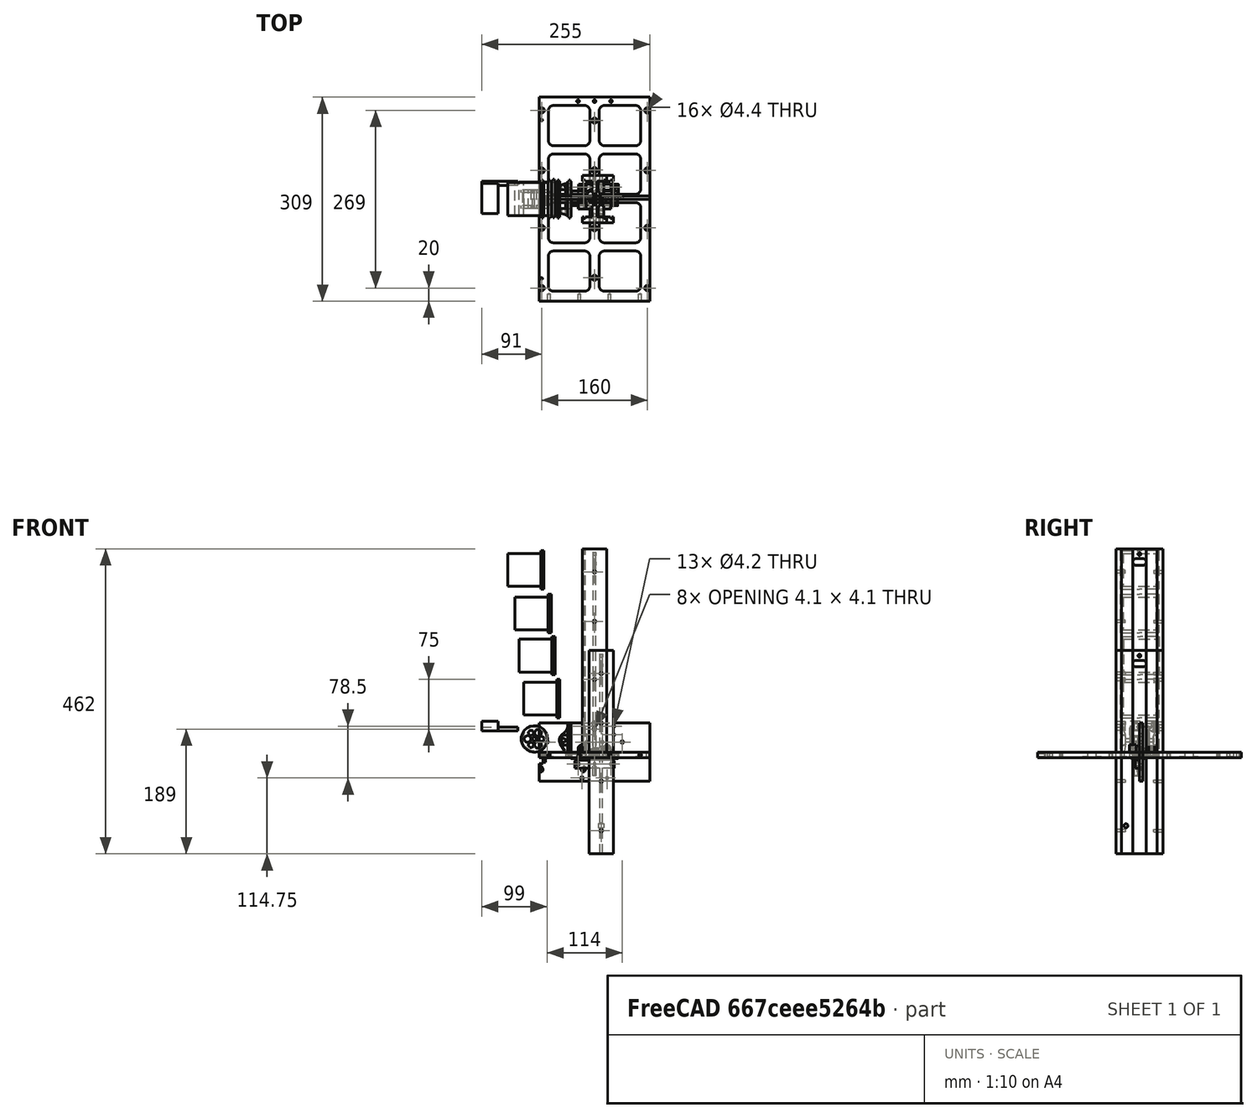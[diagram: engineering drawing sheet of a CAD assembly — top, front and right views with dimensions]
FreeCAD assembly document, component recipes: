
FREECAD ASSEMBLY — COMPONENT RECIPES ("simulation")

This assembly document has 7 components, labeled P0..P6 below (a component is one placed body or linked part). 3 of them carry a construction recipe — the FreeCAD feature program that regenerates the part from scratch, quoted from this document or its linked companion documents; the rest are supplied as boundary geometry only. No exploded tour is included for this assembly.
COMPONENT P0 — geometry summary ("door_001"; no construction recipe available for this part):
  bounding box: 168.0 x 88.5 x 8.0 mm
  tessellated surface: 8,896 triangles
  volume: 73640 mm^3 (62% of its bounding box)
COMPONENT P1 — geometry summary ("door_003"; no construction recipe available for this part):
  bounding box: 60.0 x 23.0 x 16.0 mm
  tessellated surface: 6,880 triangles
  volume: 10095 mm^3 (46% of its bounding box)
COMPONENT P2 — geometry summary ("door_004"; no construction recipe available for this part):
  bounding box: 80.0 x 5.0 x 5.0 mm
  tessellated surface: 500 triangles
  volume: 1571 mm^3 (79% of its bounding box)
  symmetry: 2-fold rotationally symmetric about the x axis; 2-fold rotationally symmetric about the y axis; 6-fold rotationally symmetric about the z axis; mirror-symmetric across its x mid-plane, y mid-plane
COMPONENT P3 — geometry summary ("door_005"; no construction recipe available for this part):
  bounding box: 16.0 x 12.0 x 8.0 mm
  tessellated surface: 15,084 triangles
  volume: 969 mm^3 (63% of its bounding box)
  symmetry: 2-fold rotationally symmetric about the z axis; mirror-symmetric across its y mid-plane
COMPONENT P4 — recipe-attached ("hinge_001", a linked part whose construction recipe lives in a companion FreeCAD document of the same project; that document's serialized recipe follows).
Construction recipe (the companion document, serialized — sketch geometry with constraints, then the solid features built on it; lengths are millimeters unless a unit is written):

FCSTD DOCUMENT  (FreeCAD 0.18R14555 (Git shallow))
Label: hinge
License: All rights reserved
LicenseURL: http://en.wikipedia.org/wiki/All_rights_reserved
objects: TechDraw::DrawViewDimension×17, Sketcher::SketchObject×11, PartDesign::Pocket×6, TechDraw::DrawProjGroupItem×6, PartDesign::Pad×3, TechDraw::DrawProjGroup×3, PartDesign::Body×3, PartDesign::Hole×2, TechDraw::DrawSVGTemplate×2, TechDraw::DrawViewAnnotation×2, TechDraw::DrawViewSymbol×2, TechDraw::DrawViewPart×2, TechDraw::DrawPage×2, PartDesign::Plane×1, PartDesign::Fillet×1, TechDraw::DrawViewSection×1
note: 38 computed .brp shape members not serialized (recipe doc carries the construction recipe); baked Part::Feature solids carry a one-line shape summary decoded from their .brp

FEATURE [Sketcher::SketchObject] Sketch001
  MapMode = 5
  Support = -> [XY_Plane001]
  sketch-geometry (8):
    g0: LineSegment StartX=-35 StartY=-10 StartZ=0 EndX=-35 EndY=12.5 EndZ=0
    g1: LineSegment StartX=-35 StartY=12.5 StartZ=0 EndX=35 EndY=12.5 EndZ=0
    g2: LineSegment StartX=35 StartY=12.5 StartZ=0 EndX=35 EndY=-10 EndZ=0
    g3: LineSegment StartX=35 StartY=-10 StartZ=0 EndX=25 EndY=-10 EndZ=0
    g4: LineSegment StartX=25 StartY=-10 StartZ=0 EndX=25 EndY=0 EndZ=0
    g5: LineSegment StartX=-35 StartY=-10 StartZ=0 EndX=-25 EndY=-10 EndZ=0
    g6: LineSegment StartX=-25 StartY=-10 StartZ=0 EndX=-25 EndY=0 EndZ=0
    g7: LineSegment StartX=-25 StartY=0 StartZ=0 EndX=25 EndY=0 EndZ=0
  constraints (22):
    c: Vertical(g0)
    c: Coincident(g0,g1)
    c: Coincident(g1,g2)
    c: Vertical(g2)
    c: Coincident(g2,g3)
    c: Horizontal(g3)
    c: Coincident(g3,g4)
    c: PointOnObject(g4,g-1)
    c: Coincident(g0,g5)
    c: Horizontal(g5)
    c: Coincident(g5,g6)
    c: PointOnObject(g6,g-1)
    c: Vertical(g6)
    c: Vertical(g4)
    c: Symmetric(g1,g0,g-2)
    c: Symmetric(g3,g5,g-2)
    c: Coincident(g7,g4)
    c: DistanceX(g5,g5) = 10
    c: DistanceY(g6,g6) = 10
    c: Coincident(g7,g6)
    c: DistanceX(g5,g3) = 50
    c: DistanceY(g-1,g1) = 12.5
FEATURE [PartDesign::Pad] Pad001
  Length = 10
  Length2 = 100
  Profile = -> Sketch001
  Reversed = true
  Type = 0
FEATURE [Sketcher::SketchObject] Sketch002
  MapMode = 5
  Placement = pos=(0,0,0) rot=(0.57735,0.57735,0.57735;2.0944rad)
  Support = -> [YZ_Plane001]
  sketch-geometry (10):
    g0: Circle CenterX=-5 CenterY=-5 CenterZ=0 NormalX=0 NormalY=0 NormalZ=1 AngleXU=0 Radius=2.5
    g1: ArcOfCircle CenterX=-5 CenterY=-5 CenterZ=0 NormalX=0 NormalY=0 NormalZ=1 AngleXU=0 Radius=5 StartAngle=1.5708 EndAngle=3.14159
    g2: LineSegment [constr] StartX=-10 StartY=-5 StartZ=0 EndX=-10 EndY=0 EndZ=0
    g3: LineSegment StartX=-10 StartY=0 StartZ=0 EndX=-5 EndY=0 EndZ=0
    g4: LineSegment StartX=-10 StartY=-10 StartZ=0 EndX=-5 EndY=-10 EndZ=0
    g5: ArcOfCircle CenterX=-5 CenterY=-5 CenterZ=0 NormalX=0 NormalY=0 NormalZ=1 AngleXU=0 Radius=5 StartAngle=3.14159 EndAngle=4.71239
    g6: LineSegment [constr] StartX=-10 StartY=-5 StartZ=0 EndX=-10 EndY=-10 EndZ=0
    g7: LineSegment StartX=-10 StartY=0 StartZ=0 EndX=-13 EndY=0 EndZ=0
    g8: LineSegment StartX=-13 StartY=0 StartZ=0 EndX=-13 EndY=-10 EndZ=0
    g9: LineSegment StartX=-13 StartY=-10 StartZ=0 EndX=-10 EndY=-10 EndZ=0
  constraints (27):
    c: Diameter(g0) = 5
    c: Coincident(g1,g0)
    c: Vertical(g2)
    c: Coincident(g3,g2)
    c: Tangent(g3,g1) = 1.5708
    c: Coincident(g1,g3)
    c: Horizontal(g3)
    c: DistanceX(g0,g-1) = 5
    c: PointOnObject(g2,g-1)
    c: DistanceY(g0,g-1) = 5
    c: Horizontal(g4)
    c: Tangent(g1,g5) = -1.5708
    c: Tangent(g1,g2) = 1.5708
    c: Coincident(g6,g1)
    c: Vertical(g6)
    c: Coincident(g4,g6)
    c: Equal(g6,g2)
    c: Coincident(g3,g7)
    c: Coincident(g7,g8)
    c: Vertical(g8)
    c: Coincident(g8,g9)
    c: Coincident(g9,g4)
    c: Horizontal(g9)
    c: Horizontal(g7)
    c: DistanceX(g1,g0) = 5
    c: DistanceX(g9,g9) = 3
    c: Tangent(g5,g4) = -1.5708
FEATURE [PartDesign::Pocket] Pocket
  BaseFeature = -> Pad001
  Length = 5
  Length2 = 100
  Midplane = true
  Profile = -> Sketch002
  Type = 1
FEATURE [Sketcher::SketchObject] Sketch007
  MapMode = 5
  Support = -> [XY_Plane001]
  sketch-geometry (5):
    g0: Circle [constr] CenterX=0 CenterY=6 CenterZ=0 NormalX=0 NormalY=0 NormalZ=1 AngleXU=0 Radius=2.1
    g1: Circle CenterX=25 CenterY=6 CenterZ=0 NormalX=0 NormalY=0 NormalZ=1 AngleXU=0 Radius=2.1
    g2: Circle CenterX=-25 CenterY=6 CenterZ=0 NormalX=0 NormalY=0 NormalZ=1 AngleXU=0 Radius=2.1
    g3: LineSegment [constr] StartX=0 StartY=6 StartZ=0 EndX=25 EndY=6 EndZ=0
    g4: LineSegment [constr] StartX=0 StartY=6 StartZ=0 EndX=-25 EndY=6 EndZ=0
  constraints (13):
    c: PointOnObject(g0,g-2)
    c: Coincident(g3,g0)
    c: Coincident(g3,g1)
    c: Coincident(g4,g0)
    c: Coincident(g4,g2)
    c: Horizontal(g3)
    c: Horizontal(g4)
    c: Equal(g4,g3)
    c: DistanceX(g2,g1) = 50
    c: Diameter(g0) = 4.2
    c: Equal(g0,g1)
    c: Equal(g0,g2)
    c: DistanceY(g-1,g0) = 6
FEATURE [PartDesign::Hole] Hole
  BaseFeature = -> Pocket
  Depth = 25
  DepthType = 1
  Diameter = 4.2
  DrillPoint = 1
  DrillPointAngle = 118
  HoleCutCountersinkAngle = 90
  HoleCutDepth = 0
  HoleCutDiameter = 0
  HoleCutType = 0
  ModelActualThread = false
  Profile = -> Sketch007
  Tapered = false
  TaperedAngle = 90
  ThreadAngle = 0
  ThreadClass = 0
  ThreadCutOffInner = 0
  ThreadCutOffOuter = 0
  ThreadDirection = 0
  ThreadFit = 0
  ThreadPitch = 0
  ThreadSize = 0
  ThreadType = 0
  Threaded = false
FEATURE [Sketcher::SketchObject] Sketch
  MapMode = 5
  Placement = pos=(0,0,0) rot=(0.57735,0.57735,0.57735;2.0944rad)
  Support = -> [YZ_Plane]
  sketch-geometry (7):
    g0: Circle CenterX=-5 CenterY=-5 CenterZ=0 NormalX=0 NormalY=0 NormalZ=1 AngleXU=0 Radius=2.5
    g1: ArcOfCircle CenterX=-5 CenterY=-5 CenterZ=0 NormalX=0 NormalY=0 NormalZ=1 AngleXU=0 Radius=5 StartAngle=4.71239 EndAngle=7.85398
    g2: LineSegment StartX=-4.99997 StartY=12 StartZ=0 EndX=-15 EndY=12 EndZ=0
    g3: LineSegment StartX=-15 StartY=12 StartZ=0 EndX=-15 EndY=-5 EndZ=0
    g4: LineSegment StartX=-9.99997 StartY=-10 StartZ=0 EndX=-5 EndY=-10 EndZ=0
    g5: LineSegment StartX=-4.99997 StartY=-8.94778e-11 StartZ=0 EndX=-4.99997 EndY=12 EndZ=0
    g6: ArcOfCircle CenterX=-9.99997 CenterY=-5 CenterZ=0 NormalX=0 NormalY=0 NormalZ=1 AngleXU=0 Radius=5 StartAngle=3.14159 EndAngle=4.71239
  constraints (20):
    c: DistanceX(g0,g-1) = 5
    c: DistanceY(g0,g-1) = 5
    c: Diameter(g0) = 5
    c: Coincident(g1,g0)
    c: PointOnObject(g1,g-1)
    c: Radius(g1) = 5
    c: Horizontal(g2)
    c: Coincident(g2,g3)
    c: Vertical(g3)
    c: Coincident(g4,g1)
    c: Horizontal(g4)
    c: DistanceY(g1,g2) = 12
    c: DistanceY(g1,g0) = 5
    c: DistanceX(g2,g2) = 10
    c: Coincident(g5,g2)
    c: Vertical(g5)
    c: Tangent(g4,g6) = -1.5708
    c: Tangent(g3,g6) = -1.5708
    c: Radius(g6) = 5
    c: Coincident(g5,g1)
FEATURE [PartDesign::Pad] Pad
  Length = 50
  Length2 = 100
  Midplane = true
  Placement = pos=(0,0,0) rot=(0.57735,0.57735,0.57735;2.0944rad)
  Profile = -> Sketch
  Type = 0
FEATURE [Sketcher::SketchObject] Sketch010
  MapMode = 5
  Placement = pos=(0,0,0) rot=(1,0,0;1.5708rad)
  Support = -> [XZ_Plane]
  sketch-geometry (14):
    g0: LineSegment StartX=13 StartY=5 StartZ=0 EndX=13 EndY=4 EndZ=0
    g1: LineSegment StartX=-13 StartY=4 StartZ=0 EndX=-13 EndY=5 EndZ=0
    g2: ArcOfCircle CenterX=-19 CenterY=5 CenterZ=0 NormalX=0 NormalY=0 NormalZ=1 AngleXU=0 Radius=6 StartAngle=1e-16 EndAngle=3.14159
    g3: ArcOfCircle CenterX=19 CenterY=5 CenterZ=0 NormalX=0 NormalY=0 NormalZ=1 AngleXU=0 Radius=6 StartAngle=0 EndAngle=3.14159
    g4: LineSegment [constr] StartX=25 StartY=5 StartZ=0 EndX=-25 EndY=5 EndZ=0
    g5: LineSegment StartX=25 StartY=5 StartZ=0 EndX=25 EndY=11 EndZ=0
    g6: LineSegment [constr] StartX=25 StartY=11 StartZ=0 EndX=-25 EndY=11 EndZ=0
    g7: LineSegment StartX=-25 StartY=11 StartZ=0 EndX=-25 EndY=5 EndZ=0
    g8: LineSegment StartX=-25 StartY=11 StartZ=0 EndX=-25 EndY=12 EndZ=0
    g9: LineSegment StartX=-25 StartY=12 StartZ=0 EndX=25 EndY=12 EndZ=0
    g10: LineSegment StartX=25 StartY=12 StartZ=0 EndX=25 EndY=11 EndZ=0
    g11: LineSegment StartX=-11 StartY=2 StartZ=0 EndX=11 EndY=2 EndZ=0
    g12: ArcOfCircle CenterX=-11 CenterY=4 CenterZ=0 NormalX=0 NormalY=0 NormalZ=1 AngleXU=0 Radius=2 StartAngle=3.14159 EndAngle=4.71239
    g13: ArcOfCircle CenterX=11 CenterY=4 CenterZ=0 NormalX=0 NormalY=0 NormalZ=1 AngleXU=0 Radius=2 StartAngle=4.71239 EndAngle=6.28319
  constraints (39):
    c: Vertical(g0)
    c: Vertical(g1)
    c: Symmetric(g0,g1,g-2)
    c: DistanceX(g1,g0) = 26
    c: Coincident(g2,g1)
    c: Coincident(g3,g0)
    c: Coincident(g4,g3)
    c: Coincident(g4,g2)
    c: Horizontal(g4)
    c: PointOnObject(g2,g4)
    c: PointOnObject(g1,g4)
    c: PointOnObject(g3,g4)
    c: Equal(g3,g2)
    c: DistanceX(g4,g4) = 50
    c: Coincident(g3,g5)
    c: Coincident(g5,g6)
    c: Horizontal(g6)
    c: Coincident(g6,g7)
    c: Coincident(g7,g2)
    c: Vertical(g7)
    c: DistanceY(g-1,g6) = 11
    c: Coincident(g7,g8)
    c: Vertical(g8)
    c: Coincident(g8,g9)
    c: Horizontal(g9)
    c: Coincident(g9,g10)
    c: Coincident(g10,g5)
    c: Vertical(g10)
    c: Vertical(g5)
    c: DistanceY(g8,g8) = 1
    c: Tangent(g2,g6)
    c: Horizontal(g11)
    c: Tangent(g1,g12) = 1.5708
    c: Tangent(g11,g12) = -1.5708
    c: Radius(g12) = 2
    c: DistanceY(g-1,g11) = 2
    c: Tangent(g0,g13) = 1.5708
    c: Tangent(g11,g13) = -1.5708
    c: Equal(g13,g12)
FEATURE [PartDesign::Plane] DatumPlane001
  AttachmentOffset = pos=(0,0,15) rot=(0,0,1;0rad)
  Length = 56.4768
  MapMode = 5
  Placement = pos=(0,-15,-3.3e-15) rot=(1,0,0;1.5708rad)
  ResizeMode = 0
  Support = -> [XZ_Plane]
  Width = 27.4512
FEATURE [Sketcher::SketchObject] Sketch011
  MapMode = 5
  Placement = pos=(0,-15,-3.3e-15) rot=(1,0,0;1.5708rad)
  Support = -> [DatumPlane001]
  sketch-geometry (2):
    g0: Circle CenterX=-19 CenterY=5 CenterZ=0 NormalX=0 NormalY=0 NormalZ=1 AngleXU=0 Radius=2
    g1: Circle CenterX=19 CenterY=5 CenterZ=0 NormalX=0 NormalY=0 NormalZ=1 AngleXU=0 Radius=2.31769
  constraints (4):
    c: Symmetric(g1,g0,g-2)
    c: DistanceX(g0,g1) = 38
    c: Diameter(g0) = 4
    c: DistanceY(g-1,g0) = 5
FEATURE [Sketcher::SketchObject] Sketch009
  MapMode = 5
  Placement = pos=(0,0,0) rot=(1,0,0;1.5708rad)
  Support = -> [XZ_Plane]
  sketch-geometry (6):
    g0: LineSegment StartX=-11.0007 StartY=0 StartZ=0 EndX=10.9993 EndY=0 EndZ=0
    g1: LineSegment StartX=12.9993 StartY=-2 StartZ=0 EndX=12.9993 EndY=-18.3189 EndZ=0
    g2: LineSegment StartX=12.9993 StartY=-18.3189 StartZ=0 EndX=-13.0007 EndY=-18.3189 EndZ=0
    g3: LineSegment StartX=-13.0007 StartY=-18.3189 StartZ=0 EndX=-13.0007 EndY=-2 EndZ=0
    g4: ArcOfCircle CenterX=10.9993 CenterY=-2 CenterZ=0 NormalX=0 NormalY=0 NormalZ=1 AngleXU=0 Radius=2 StartAngle=0 EndAngle=1.5708
    g5: ArcOfCircle CenterX=-11.0007 CenterY=-2 CenterZ=0 NormalX=0 NormalY=0 NormalZ=1 AngleXU=0 Radius=2 StartAngle=1.5708 EndAngle=3.14159
  constraints (14):
    c: Coincident(g1,g2)
    c: Coincident(g2,g3)
    c: Horizontal(g2)
    c: Vertical(g1)
    c: Vertical(g3)
    c: Tangent(g1,g4) = 1.5708
    c: Tangent(g0,g4) = 1.5708
    c: Tangent(g0,g5) = 1.5708
    c: Tangent(g3,g5) = 1.5708
    c: DistanceX(g3,g1) = 26
    c: Radius(g4) = 2
    c: Equal(g4,g5)
    c: Horizontal(g0)
    c: PointOnObject(g0,g-1)
FEATURE [PartDesign::Pocket] Pocket002
  BaseFeature = -> Pad
  Length = 10
  Length2 = 100
  Placement = pos=(0,0,0) rot=(0.57735,0.57735,0.57735;2.0944rad)
  Profile = -> Sketch009
  Reversed = true
  Type = 0
FEATURE [PartDesign::Pocket] Pocket003
  BaseFeature = -> Pocket002
  Length = 5
  Length2 = 100
  Placement = pos=(0,0,0) rot=(0.57735,0.57735,0.57735;2.0944rad)
  Profile = -> Sketch010
  Reversed = true
  Type = 1
FEATURE [TechDraw::DrawSVGTemplate] Template
  EditableTexts = Designed_by_Name=Papamatthaiou M.; FC-Date=17/01/2020; FC-SC=1:1; FC-SHEET=1/1; FC-Title=PocketQube Static Hinge; MATERIAL=NOTE-4; REV=B; ROUGHNESS=-; Subtitle=StatikHinge; TOLERANCES=DIN ISO 2768-mk; Weight=~26.56g
  Height = 210
  Orientation = 1
  Width = 297
FEATURE [TechDraw::DrawProjGroup] ProjGroup
  AutoDistribute = true
  LockPosition = false
  ProjectionType = 1
  Rotation = 0
  ScaleType = 2
  X = 168.228
  Y = 97.2357
  spacingX = 15
  spacingY = 15
FEATURE [TechDraw::DrawViewAnnotation] Annotation
  Font = DejaVu Sans
  LineSpace = 80
  LockPosition = false
  MaxWidth = -1
  Rotation = 0
  ScaleType = 0
  Text = Notes: | 1. Drill hole \u23004.2 THRU | 2. Mating hole (H7) for part P/N:  | MISUMI  SCLGN5-70 Shaft Dia. D: 5.00,  | Tolerance: g6 (sliding fit) | 3. This part is mating with parts DoorHinge | and with y-plate | 4. Material: Al 7075 | 5. Drill hole \u23001.5 THRU. Mating holes  | for torsional springs
  TextSize = 6
  TextStyle = 0
  X = 77.2478
  Y = 49.013
FEATURE [PartDesign::Hole] Hole001
  BaseFeature = -> Pocket003
  Depth = 25
  DepthType = 1
  Diameter = 4.5
  DrillPoint = 1
  DrillPointAngle = 118
  HoleCutCountersinkAngle = 90
  HoleCutDepth = 4.6
  HoleCutDiameter = 8
  HoleCutType = 1
  ModelActualThread = false
  Placement = pos=(0,0,0) rot=(0.57735,0.57735,0.57735;2.0944rad)
  Profile = -> Sketch011
  Tapered = false
  TaperedAngle = 90
  ThreadAngle = 0
  ThreadClass = 0
  ThreadCutOffInner = 0
  ThreadCutOffOuter = 0
  ThreadDirection = 0
  ThreadFit = 0
  ThreadPitch = 0
  ThreadSize = 0
  ThreadType = 0
  Threaded = false
FEATURE [TechDraw::DrawSVGTemplate] Template001
  EditableTexts = Designed_by_Name=Papamatthaiou M.; FC-Date=17/01/2020; FC-SC=1:1; FC-SHEET=1/1; FC-Title=PocketQube Door Hinge; MATERIAL=NOTE-5; REV=B; ROUGHNESS=-; Subtitle=DoorHinge; TOLERANCES=DIN ISO 2768-mk; Weight=~17.21g
  Height = 210
  Orientation = 1
  Width = 297
FEATURE [TechDraw::DrawViewSymbol] Symbol
  LockPosition = false
  Rotation = 0
  ScaleType = 2
  Symbol = <blob: 3150 chars omitted>
  X = 16.0884
  Y = 131.565
FEATURE [TechDraw::DrawViewSymbol] Symbol001
  LockPosition = false
  Rotation = 0
  ScaleType = 2
  Symbol = <blob: 3150 chars omitted>
  X = 22.4016
  Y = 147.366
FEATURE [TechDraw::DrawViewAnnotation] Annotation001
  Font = DejaVu Sans
  LineSpace = 80
  LockPosition = false
  MaxWidth = -1
  Rotation = 0
  ScaleType = 0
  Text = Notes: | 1. Drill hole \u23004.5 THRU | 2. Mating hole (H7) for part P/N:  | MISUMI  SCLGN5-70 Shaft Dia. D: 5.00,  | Tolerance: g6 (sliding fit) | 3. This part is mating with parts DoorHinge | and with door | 4. CBORE \u23008.00 DEEP 4.6 (M4 DIN912) | 5. Material: Al 7075 | 6. Drill Holes \u23001.5 THRU. Mating | holes for torsional springs
  TextSize = 6
  TextStyle = 0
  X = 77.0938
  Y = 51.4062
FEATURE [Sketcher::SketchObject] Sketch012
  MapMode = 5
  Placement = pos=(0,0,0) rot=(1,0,0;1.5708rad)
  Support = -> [XZ_Plane001]
  sketch-geometry (3):
    g0: Circle CenterX=-1.5 CenterY=-6.9 CenterZ=0 NormalX=0 NormalY=0 NormalZ=1 AngleXU=0 Radius=0.75
    g1: Circle CenterX=1.5 CenterY=-6.9 CenterZ=0 NormalX=0 NormalY=0 NormalZ=1 AngleXU=0 Radius=0.75
    g2: GeomPoint X=0 Y=-10 Z=0
  constraints (7):
    c: Diameter(g1) = 1.5
    c: Equal(g1,g0)
    c: Symmetric(g1,g0,g-2)
    c: DistanceX(g0,g1) = 3
    c: PointOnObject(g2,g-2)
    c: DistanceY(g2,g-1) = 10
    c: DistanceY(g2,g1) = 3.1
FEATURE [PartDesign::Pocket] Pocket004
  BaseFeature = -> Hole
  Length = 9
  Length2 = 100
  Profile = -> Sketch012
  Type = 0
FEATURE [PartDesign::Fillet] Fillet
  Base = -> Pocket004 [Edge19]
  BaseFeature = -> Pocket004
  Radius = 4
FEATURE [PartDesign::Body] Body001  label="StatikHinge"
  Group = -> [Sketch001,Pad001,Sketch002,Pocket,Sketch007,Hole,Sketch012,Pocket004,Fillet]
  Origin = -> Origin001
  Tip = -> Fillet
FEATURE [TechDraw::DrawViewPart] View
  CoarseView = false
  Direction = (0.831,-0.177,0.527)
  Focus = 100
  HardHidden = false
  IsoCount = 0
  IsoHidden = false
  IsoVisible = false
  LockPosition = false
  Perspective = false
  Rotation = 0
  ScaleType = 0
  SeamHidden = false
  SeamVisible = false
  SmoothHidden = false
  SmoothVisible = false
  Source = -> [Body001]
  X = 260.762
  Y = 173.153
FEATURE [Sketcher::SketchObject] Sketch013
  MapMode = 5
  Support = -> [XY_Plane]
  sketch-geometry (2):
    g0: Circle CenterX=-12.15 CenterY=-9.2 CenterZ=0 NormalX=0 NormalY=0 NormalZ=1 AngleXU=0 Radius=0.75
    g1: Circle CenterX=12.15 CenterY=-9.2 CenterZ=0 NormalX=0 NormalY=0 NormalZ=1 AngleXU=0 Radius=0.75
  constraints (5):
    c: Diameter(g1) = 1.5
    c: Equal(g1,g0)
    c: Symmetric(g0,g1,g-2)
    c: DistanceX(g0,g1) = 24.3
    c: DistanceY(g1,g-1) = 9.2
FEATURE [PartDesign::Pocket] Pocket005
  BaseFeature = -> Hole001
  Length = 5
  Length2 = 100
  Midplane = true
  Placement = pos=(0,0,0) rot=(0.57735,0.57735,0.57735;2.0944rad)
  Profile = -> Sketch013
  Type = 1
FEATURE [PartDesign::Body] Body  label="DoorHinge"
  Group = -> [Sketch,Pad,Sketch009,Pocket002,Sketch010,Pocket003,DatumPlane001,Sketch011,Hole001,Sketch013,Pocket005]
  Origin = -> Origin
  Tip = -> Pocket005
FEATURE [TechDraw::DrawProjGroupItem] ProjItem002  label="Front001"
  CoarseView = false
  Direction = (0,1,0)
  Focus = 100
  HardHidden = false
  IsoCount = 0
  IsoHidden = false
  IsoVisible = false
  LockPosition = true
  Perspective = false
  Rotation = 0
  RotationVector = (-1,0,0)
  ScaleType = 2
  SeamHidden = false
  SeamVisible = false
  SmoothHidden = false
  SmoothVisible = false
  Source = -> [Body]
  Type = 0
  X = 0
  Y = 0
FEATURE [TechDraw::DrawProjGroupItem] ProjItem003  label="Left001"
  CoarseView = false
  Direction = (1,1e-16,0)
  Focus = 100
  HardHidden = false
  IsoCount = 0
  IsoHidden = false
  IsoVisible = false
  LockPosition = false
  Perspective = false
  Rotation = 0
  RotationVector = (-1e-16,1,0)
  ScaleType = 2
  SeamHidden = false
  SeamVisible = false
  SmoothHidden = false
  SmoothVisible = false
  Source = -> [Body]
  Type = 1
  X = 65
  Y = 0
FEATURE [TechDraw::DrawViewDimension] Dimension007
  Arbitrary = false
  FormatSpec = (Note-1) ⌀%.2f
  LockPosition = false
  MeasureType = 1
  OverTolerance = 0
  References2D = -> [ProjItem002]
  Rotation = 0
  ScaleType = 0
  Type = 5
  UnderTolerance = 0
  X = 5.54075
  Y = 26.0395
FEATURE [TechDraw::DrawViewDimension] Dimension008
  Arbitrary = false
  FormatSpec = (Note-2) ⌀%.2fH7
  LockPosition = false
  MeasureType = 1
  OverTolerance = 0
  References2D = -> [ProjItem003]
  Rotation = 0
  ScaleType = 0
  Type = 5
  UnderTolerance = 0
  X = 38.605
  Y = 5.77784
FEATURE [TechDraw::DrawViewPart] View002
  CoarseView = false
  Direction = (-0.669,0.732,-0.128)
  Focus = 100
  HardHidden = false
  IsoCount = 0
  IsoHidden = false
  IsoVisible = false
  LockPosition = false
  Perspective = false
  Rotation = 0
  ScaleType = 0
  SeamHidden = false
  SeamVisible = false
  SmoothHidden = false
  SmoothVisible = false
  Source = -> [Body]
  X = 259.541
  Y = 183.599
FEATURE [TechDraw::DrawViewSection] DrawViewSection  label="Section B - B"
  BaseView = -> ProjItem002
  CoarseView = false
  Direction = (1,0,0)
  FileHatchPattern = <path>
  Focus = 100
  FuseBeforeCut = true
  HardHidden = false
  HatchScale = 1
  IsoCount = 0
  IsoHidden = false
  IsoVisible = false
  LockPosition = false
  NameGeomPattern = Diamond
  Perspective = false
  Rotation = 0
  ScaleType = 0
  SeamHidden = false
  SeamVisible = false
  SectionDirection = 0
  SectionNormal = (1,0,0)
  SectionOrigin = (-19,-7.5,0.5)
  SectionSymbol = B
  SmoothHidden = false
  SmoothVisible = false
  Source = -> [Body]
  X = 240.508
  Y = 105.408
FEATURE [TechDraw::DrawViewDimension] Dimension010
  Arbitrary = false
  FormatSpec = (Note-4) %.2f
  LockPosition = false
  MeasureType = 1
  OverTolerance = 0
  References2D = -> [DrawViewSection]
  Rotation = 0
  ScaleType = 0
  Type = 2
  UnderTolerance = 0
  X = -32.2034
  Y = -16.2929
FEATURE [TechDraw::DrawProjGroupItem] ProjItem004  label="Front002"
  CoarseView = false
  Direction = (0,0,1)
  Focus = 100
  HardHidden = false
  IsoCount = 0
  IsoHidden = false
  IsoVisible = false
  LockPosition = true
  Perspective = false
  Rotation = 0
  RotationVector = (1,0,0)
  ScaleType = 2
  SeamHidden = false
  SeamVisible = false
  SmoothHidden = false
  SmoothVisible = false
  Source = -> [Fillet]
  Type = 0
  X = 0
  Y = 0
FEATURE [TechDraw::DrawProjGroupItem] ProjItem005  label="Left002"
  CoarseView = false
  Direction = (-1,0,1e-16)
  Focus = 100
  HardHidden = false
  IsoCount = 0
  IsoHidden = false
  IsoVisible = false
  LockPosition = false
  Perspective = false
  Rotation = 0
  RotationVector = (1e-16,0,1)
  ScaleType = 2
  SeamHidden = false
  SeamVisible = false
  SmoothHidden = false
  SmoothVisible = false
  Source = -> [Fillet]
  Type = 1
  X = 85
  Y = 0
FEATURE [TechDraw::DrawViewDimension] Dimension012
  Arbitrary = false
  FormatSpec = (Note-3) %.2f
  LockPosition = false
  MeasureType = 1
  OverTolerance = 0.1
  References2D = -> [ProjItem004]
  Rotation = 0
  ScaleType = 0
  Type = 1
  UnderTolerance = 0
  X = -1.46419
  Y = -24.1349
FEATURE [TechDraw::DrawViewDimension] Dimension013
  Arbitrary = false
  FormatSpec = %.2f
  LockPosition = false
  MeasureType = 1
  OverTolerance = 0
  References2D = -> [ProjItem004]
  Rotation = 0
  ScaleType = 0
  Type = 1
  UnderTolerance = -0.2
  X = -2.04987
  Y = -35.5556
FEATURE [TechDraw::DrawProjGroupItem] ProjItem006  label="Bottom"
  CoarseView = false
  Direction = (0,-1,0)
  Focus = 100
  HardHidden = false
  IsoCount = 0
  IsoHidden = false
  IsoVisible = false
  LockPosition = false
  Perspective = false
  Rotation = 0
  RotationVector = (1,0,0)
  ScaleType = 2
  SeamHidden = false
  SeamVisible = false
  SmoothHidden = false
  SmoothVisible = false
  Source = -> [Fillet]
  Type = 5
  X = 0
  Y = 37.5
FEATURE [TechDraw::DrawProjGroup] ProjGroup002
  Anchor = -> ProjItem004
  AutoDistribute = true
  LockPosition = false
  ProjectionType = 1
  Rotation = 0
  ScaleType = 2
  Source = -> [Fillet]
  Views = -> [ProjItem004,ProjItem005,ProjItem006]
  X = 88.691
  Y = 138.45
  spacingX = 15
  spacingY = 15
FEATURE [TechDraw::DrawViewDimension] Dimension014
  Arbitrary = false
  FormatSpec = (Note-1) ⌀%.2f 
  LockPosition = false
  MeasureType = 1
  OverTolerance = 0
  References2D = -> [ProjItem004]
  Rotation = 0
  ScaleType = 0
  Type = 5
  UnderTolerance = 0
  X = 0.44554
  Y = 19.6037
FEATURE [TechDraw::DrawViewDimension] Dimension015
  Arbitrary = false
  FormatSpec = (Note-2) ⌀%.2fH7
  LockPosition = false
  MeasureType = 1
  OverTolerance = 0
  References2D = -> [ProjItem005]
  Rotation = 0
  ScaleType = 0
  Type = 5
  UnderTolerance = 0
  X = 32.9699
  Y = 6.01477
FEATURE [TechDraw::DrawViewDimension] Dimension016
  Arbitrary = false
  FormatSpec = %.2f
  LockPosition = false
  MeasureType = 1
  OverTolerance = 0.1
  References2D = -> [ProjItem005]
  Rotation = 0
  ScaleType = 0
  Type = 2
  UnderTolerance = -0.1
  X = -21.2176
  Y = 29.9006
FEATURE [TechDraw::DrawViewDimension] Dimension
  Arbitrary = false
  FormatSpec = %.2f
  LockPosition = false
  MeasureType = 1
  OverTolerance = 0.1
  References2D = -> [ProjItem006]
  Rotation = 0
  ScaleType = 0
  Type = 2
  UnderTolerance = 0
  X = -59.5871
  Y = 7.81223
FEATURE [TechDraw::DrawViewDimension] Dimension017
  Arbitrary = false
  FormatSpec = %.2f
  LockPosition = false
  MeasureType = 1
  OverTolerance = 0.1
  References2D = -> [ProjItem006]
  Rotation = 0
  ScaleType = 0
  Type = 1
  UnderTolerance = -0.1
  X = -20.6451
  Y = 17.6805
FEATURE [TechDraw::DrawViewDimension] Dimension018
  Arbitrary = false
  FormatSpec = (Note-5) ⌀%.2f
  LockPosition = false
  MeasureType = 1
  OverTolerance = 0
  References2D = -> [ProjItem006]
  Rotation = 0
  ScaleType = 0
  Type = 5
  UnderTolerance = 0
  X = 34.1246
  Y = 16.7219
FEATURE [TechDraw::DrawPage] Page
  KeepUpdated = true
  ProjectionType = 0
  Template = -> Template
  Views = -> [ProjGroup,View,Annotation,Symbol,ProjGroup002,Dimension012,Dimension013,Dimension014,Dimension015,Dimension016,Dimension,Dimension017,Dimension018]
FEATURE [TechDraw::DrawProjGroupItem] ProjItem007  label="Top"
  CoarseView = false
  Direction = (0,0,1)
  Focus = 100
  HardHidden = false
  IsoCount = 0
  IsoHidden = false
  IsoVisible = false
  LockPosition = true
  Perspective = false
  Rotation = 0
  RotationVector = (-1,0,0)
  ScaleType = 2
  SeamHidden = false
  SeamVisible = false
  SmoothHidden = false
  SmoothVisible = false
  Source = -> [Body]
  Type = 4
  X = 0
  Y = -42.1726
FEATURE [TechDraw::DrawProjGroup] ProjGroup001
  Anchor = -> ProjItem002
  AutoDistribute = true
  LockPosition = false
  ProjectionType = 1
  Rotation = 0
  ScaleType = 2
  Source = -> [Body]
  Views = -> [ProjItem002,ProjItem003,ProjItem007]
  X = 86.3263
  Y = 154.205
  spacingX = 15
  spacingY = 15
FEATURE [TechDraw::DrawViewDimension] Dimension019
  Arbitrary = false
  FormatSpec = (Note-3) %.2f
  LockPosition = false
  MeasureType = 1
  OverTolerance = 0
  References2D = -> [ProjItem002]
  Rotation = 0
  ScaleType = 0
  Type = 1
  UnderTolerance = -0.1
  X = -2.96872
  Y = -23.0803
FEATURE [TechDraw::DrawViewDimension] Dimension020
  Arbitrary = false
  FormatSpec = (Note-3) R%.2f
  LockPosition = false
  MeasureType = 1
  OverTolerance = 0
  References2D = -> [ProjItem003]
  Rotation = 0
  ScaleType = 0
  Type = 4
  UnderTolerance = -0.1
  X = 39.0019
  Y = -15.3008
FEATURE [TechDraw::DrawViewDimension] Dimension021
  Arbitrary = false
  FormatSpec = %.2f
  LockPosition = false
  MeasureType = 1
  OverTolerance = 0.1
  References2D = -> [ProjItem007]
  Rotation = 0
  ScaleType = 0
  Type = 1
  UnderTolerance = 0
  X = 3.06171
  Y = -19.944
FEATURE [TechDraw::DrawViewDimension] Dimension022
  Arbitrary = false
  FormatSpec = %.2f
  LockPosition = false
  MeasureType = 1
  OverTolerance = 0.1
  References2D = -> [ProjItem007]
  Rotation = 0
  ScaleType = 0
  Type = 2
  UnderTolerance = -0.1
  X = -52.0507
  Y = -9.25974
FEATURE [TechDraw::DrawViewDimension] Dimension023
  Arbitrary = false
  FormatSpec = (Note-6) ⌀%.2f
  LockPosition = false
  MeasureType = 1
  OverTolerance = 0
  References2D = -> [ProjItem007]
  Rotation = 0
  ScaleType = 0
  Type = 5
  UnderTolerance = 0
  X = 48.8253
  Y = 8.96625
FEATURE [TechDraw::DrawViewDimension] Dimension024
  Arbitrary = false
  FormatSpec = %.2f
  LockPosition = false
  MeasureType = 1
  OverTolerance = 0.1
  References2D = -> [DrawViewSection]
  Rotation = 0
  ScaleType = 0
  Type = 2
  UnderTolerance = -0.1
  X = 14.5552
  Y = 19.9011
FEATURE [TechDraw::DrawPage] Page001
  KeepUpdated = true
  ProjectionType = 0
  Template = -> Template001
  Views = -> [ProjGroup001,Dimension007,Dimension008,Symbol001,View002,Annotation001,DrawViewSection,Dimension010,Dimension019,Dimension020,Dimension021,Dimension022,Dimension023,Dimension024]
FEATURE [Sketcher::SketchObject] Sketch014
  MapMode = 5
  Placement = pos=(0,0,0) rot=(0.57735,0.57735,0.57735;2.0944rad)
  Support = -> [YZ_Plane002]
  sketch-geometry (1):
    g0: Circle CenterX=0 CenterY=0 CenterZ=0 NormalX=0 NormalY=0 NormalZ=1 AngleXU=0 Radius=2.5
  constraints (2):
    c: Coincident(g0,g-1)
    c: Diameter(g0) = 5
FEATURE [PartDesign::Pad] Pad002
  Length = 80
  Length2 = 100
  Midplane = true
  Placement = pos=(0,0,0) rot=(0.57735,0.57735,0.57735;2.0944rad)
  Profile = -> Sketch014
  Type = 0
FEATURE [Sketcher::SketchObject] Sketch015
  MapMode = 5
  Support = -> [XY_Plane002]
  sketch-geometry (4):
    g0: Circle CenterX=36.25 CenterY=0 CenterZ=0 NormalX=0 NormalY=0 NormalZ=1 AngleXU=0 Radius=0.75
    g1: Circle CenterX=-36.25 CenterY=0 CenterZ=0 NormalX=0 NormalY=0 NormalZ=1 AngleXU=0 Radius=0.75
    g2: GeomPoint X=-35.5 Y=0 Z=0
    g3: GeomPoint X=35.5 Y=0 Z=0
  constraints (9):
    c: PointOnObject(g0,g-1)
    c: PointOnObject(g1,g-1)
    c: PointOnObject(g2,g-1)
    c: PointOnObject(g3,g0)
    c: PointOnObject(g2,g1)
    c: Symmetric(g2,g3,g-2)
    c: DistanceX(g2,g3) = 71
    c: Diameter(g1) = 1.5
    c: Equal(g1,g0)
FEATURE [PartDesign::Pocket] Pocket006
  BaseFeature = -> Pad002
  Length = 5
  Length2 = 100
  Midplane = true
  Placement = pos=(0,0,0) rot=(0.57735,0.57735,0.57735;2.0944rad)
  Profile = -> Sketch015
  Type = 1
FEATURE [PartDesign::Body] Body002  label="Pin"
  Group = -> [Sketch014,Pad002,Sketch015,Pocket006]
  Origin = -> Origin002
  Tip = -> Pocket006
note: 1 file-system path scrubbed to <path> (originals preserved in the JSON sidecar)
COMPONENT P5 — same part as P4; its construction recipe is shown at P4.
COMPONENT P6 — recipe-attached ("rail_001", a linked part whose construction recipe lives in a companion FreeCAD document of the same project; that document's serialized recipe follows).
Construction recipe (the companion document, serialized — sketch geometry with constraints, then the solid features built on it; lengths are millimeters unless a unit is written):

FCSTD DOCUMENT  (FreeCAD 0.19R)
Label: deployer-rail
License: Creative Commons Attribution-ShareAlike
LicenseURL: http://creativecommons.org/licenses/by-sa/4.0/
objects: TechDraw::DrawViewDimension×12, TechDraw::DrawViewBalloon×3, TechDraw::DrawViewSection×2, TechDraw::DrawViewAnnotation×2, TechDraw::DrawViewSymbol×2, Part::Feature×1, TechDraw::DrawSVGTemplate×1, TechDraw::DrawProjGroupItem×1, TechDraw::DrawProjGroup×1, TechDraw::DrawViewPart×1, TechDraw::DrawPage×1
note: 1 computed .brp shape members not serialized (recipe doc carries the construction recipe); baked Part::Feature solids carry a one-line shape summary decoded from their .brp

FEATURE [Part::Feature] Solid  label="Deployer_Rail"
  shape: bbox 37 x 71.5 x 308 mm, 82 faces (baked)
FEATURE [TechDraw::DrawSVGTemplate] Template
  EditableTexts = Designed_by_Name=A. Ampatzoglou; FC-Date=30/10/2019; FC-SC=1:2; FC-SHEET=1/1; FC-Title=PocketQube - Deployer Rail; MATERIAL=NOTE-2; REV=A; ROUGHNESS=-; Subtitle=Deployer Rail; TOLERANCES=DIN ISO 2768- mk; Weight=N/A
  Height = 210
  Orientation = 1
  Width = 297
FEATURE [TechDraw::DrawProjGroupItem] ProjItem  label="Front"
  CoarseView = false
  Direction = (0,-1,0)
  Focus = 100
  HardHidden = false
  IsoCount = 0
  IsoHidden = false
  IsoVisible = false
  LockPosition = true
  Perspective = false
  Rotation = 0
  RotationVector = (1,0,0)
  Scale = 0.5
  ScaleType = 2
  SeamHidden = false
  SeamVisible = false
  SmoothHidden = false
  SmoothVisible = false
  Source = -> [Solid]
  Type = 0
  X = 0
  Y = 0
FEATURE [TechDraw::DrawProjGroup] ProjGroup
  Anchor = -> ProjItem
  AutoDistribute = true
  LockPosition = false
  ProjectionType = 1
  Rotation = 0
  Scale = 0.5
  ScaleType = 2
  Source = -> [Solid]
  Views = -> [ProjItem]
  X = 44.12
  Y = 115.109
  spacingX = 15
  spacingY = 15
FEATURE [TechDraw::DrawViewSection] DrawViewSection  label="             A - A"
  BaseView = -> ProjItem
  CoarseView = false
  Direction = (0,0,-1)
  Focus = 100
  FuseBeforeCut = true
  HardHidden = false
  HatchScale = 1
  IsoCount = 0
  IsoHidden = false
  IsoVisible = false
  LockPosition = false
  NameGeomPattern = Diamond
  Perspective = false
  Rotation = 0
  ScaleType = 0
  SeamHidden = false
  SeamVisible = false
  SectionDirection = 2
  SectionNormal = (0,0,-1)
  SectionOrigin = (4,0,-44)
  SectionSymbol = A
  SmoothHidden = false
  SmoothVisible = false
  Source = -> [Solid]
  X = 199.175
  Y = 152.259
FEATURE [TechDraw::DrawViewPart] View
  CoarseView = false
  Direction = (0.3,0.1,0.5)
  Focus = 100
  HardHidden = false
  IsoCount = 0
  IsoHidden = false
  IsoVisible = false
  LockPosition = false
  Perspective = false
  Rotation = 0
  Scale = 0.5
  ScaleType = 0
  SeamHidden = false
  SeamVisible = false
  SmoothHidden = false
  SmoothVisible = false
  Source = -> [Solid]
  X = 263.537
  Y = 126.234
FEATURE [TechDraw::DrawViewAnnotation] Annotation001
  Font = DejaVu Sans
  LineSpace = 80
  LockPosition = false
  MaxWidth = -1
  Rotation = 0
  ScaleType = 0
  Text = SCALE 1:1
  TextSize = 6
  TextStyle = 0
  X = 218.818
  Y = 193.05
FEATURE [TechDraw::DrawViewDimension] Dimension
  Arbitrary = false
  FormatSpec = %.2f
  Inverted = false
  LockPosition = false
  MeasureType = 1
  OverTolerance = 0.1
  References2D = -> [DrawViewSection]
  Rotation = 0
  ScaleType = 0
  TheoreticalExact = false
  Type = 2
  UnderTolerance = 0
  X = -31.5648
  Y = 1.56778
FEATURE [TechDraw::DrawViewDimension] Dimension001
  Arbitrary = false
  FormatSpec = %.2f
  Inverted = false
  LockPosition = false
  MeasureType = 1
  OverTolerance = 0
  References2D = -> [DrawViewSection]
  Rotation = 0
  ScaleType = 0
  TheoreticalExact = false
  Type = 2
  UnderTolerance = -0.3
  X = -43.1748
  Y = 1.82907
FEATURE [TechDraw::DrawViewDimension] Dimension002
  Arbitrary = false
  FormatSpec = %.2f
  Inverted = false
  LockPosition = false
  MeasureType = 1
  OverTolerance = 0.1
  References2D = -> [DrawViewSection]
  Rotation = 0
  ScaleType = 0
  TheoreticalExact = false
  Type = 2
  UnderTolerance = -0.1
  X = -51.9459
  Y = 0.522592
FEATURE [TechDraw::DrawViewDimension] Dimension003
  Arbitrary = false
  FormatSpec = %.2f
  Inverted = false
  LockPosition = false
  MeasureType = 1
  OverTolerance = 0
  References2D = -> [DrawViewSection]
  Rotation = 0
  ScaleType = 0
  TheoreticalExact = false
  Type = 1
  UnderTolerance = -0.1
  X = 28.2216
  Y = 24.2303
FEATURE [TechDraw::DrawViewDimension] Dimension004
  Arbitrary = false
  FormatSpec = %.2f
  Inverted = false
  LockPosition = false
  MeasureType = 1
  OverTolerance = 0
  References2D = -> [DrawViewSection]
  Rotation = 0
  ScaleType = 0
  TheoreticalExact = false
  Type = 2
  UnderTolerance = -0.2
  X = 27.2469
  Y = -24.2361
FEATURE [TechDraw::DrawViewSymbol] Symbol
  LockPosition = false
  Rotation = 0
  Scale = 0.05
  ScaleType = 2
  Symbol = <blob: 6205 chars omitted>
  X = 109.248
  Y = 23.1847
FEATURE [TechDraw::DrawViewDimension] Dimension006
  Arbitrary = false
  FormatSpec = %.2f
  Inverted = false
  LockPosition = false
  MeasureType = 1
  OverTolerance = 0.3
  References2D = -> [ProjItem]
  Rotation = 0
  ScaleType = 0
  TheoreticalExact = false
  Type = 2
  UnderTolerance = -0.3
  X = -32.7325
  Y = -9.67052
FEATURE [TechDraw::DrawViewDimension] Dimension007
  Arbitrary = false
  FormatSpec = %.2f
  Inverted = false
  LockPosition = false
  MeasureType = 1
  OverTolerance = 0.3
  References2D = -> [ProjItem]
  Rotation = 0
  ScaleType = 0
  TheoreticalExact = false
  Type = 2
  UnderTolerance = -0.3
  X = -24.0741
  Y = -9.89304
FEATURE [TechDraw::DrawViewBalloon] Balloon
  EndType = 0
  LockPosition = false
  OriginIsSet = false
  OriginX = -7.76162
  OriginY = 358.874
  Rotation = 0
  ScaleType = 0
  Symbol = 6
  SymbolScale = 1
  Text = B
  TextWrapLen = -1
  X = -12.3107
  Y = -41.5064
  sourceView = -> DrawViewSection
FEATURE [TechDraw::DrawViewBalloon] Balloon001
  EndType = 0
  LockPosition = false
  OriginIsSet = false
  OriginX = -5.96691
  OriginY = -354.271
  Rotation = 0
  ScaleType = 0
  Symbol = 6
  SymbolScale = 1
  Text =    ⌀0.1 B
  TextWrapLen = -1
  X = -25.6388
  Y = 43.0873
  sourceView = -> DrawViewSection
FEATURE [TechDraw::DrawViewSymbol] Symbol001
  LockPosition = false
  Rotation = 0
  ScaleType = 2
  Symbol = <blob: 3150 chars omitted>
  X = 174.639
  Y = 193.03
FEATURE [TechDraw::DrawViewAnnotation] Annotation002
  Font = DejaVu Sans
  LineSpace = 80
  LockPosition = false
  MaxWidth = -1
  Rotation = 0
  ScaleType = 0
  Text = Notes: | 1. Drill Hole \u23004.1 for M4x0.7 HELICOIL | insert 2D | 2. Material: AL7075 | 3. This part is mating with part | P/N: pusher | 4. Drill Hole \u23004.5 THRU | 5. Pocket radius and width are | controlled by tool, R5 - Typical | 6. Drill hole \u23006 for part  P/N: | MISUMI 22370.0023
  TextSize = 4
  TextStyle = 0
  X = 192.567
  Y = 81.9849
FEATURE [TechDraw::DrawViewSection] DrawViewSection001  label="                  C - C"
  BaseView = -> ProjItem
  CoarseView = false
  Direction = (1,0,0)
  Focus = 100
  FuseBeforeCut = true
  HardHidden = false
  HatchScale = 1
  IsoCount = 0
  IsoHidden = false
  IsoVisible = false
  LockPosition = false
  NameGeomPattern = Diamond
  Perspective = false
  Rotation = 0
  Scale = 0.5
  ScaleType = 2
  SeamHidden = false
  SeamVisible = false
  SectionDirection = 1
  SectionNormal = (1,0,0)
  SectionOrigin = (15,-4,4)
  SectionSymbol = C
  SmoothHidden = false
  SmoothVisible = false
  Source = -> [Solid]
  X = 97.74
  Y = 119.232
FEATURE [TechDraw::DrawViewDimension] Dimension008
  Arbitrary = false
  FormatSpec = (Note-1) 8X ⌀%.2f     14
  Inverted = false
  LockPosition = false
  MeasureType = 1
  OverTolerance = 0
  References2D = -> [ProjItem]
  Rotation = 0
  ScaleType = 0
  TheoreticalExact = false
  Type = 5
  UnderTolerance = 0
  X = 45.7838
  Y = -92.4063
FEATURE [TechDraw::DrawViewDimension] Dimension009
  Arbitrary = false
  FormatSpec = (Note-6) ⌀%.2f
  Inverted = false
  LockPosition = false
  MeasureType = 1
  OverTolerance = 0
  References2D = -> [DrawViewSection001]
  Rotation = 0
  ScaleType = 0
  TheoreticalExact = false
  Type = 5
  UnderTolerance = 0
  X = 35.4993
  Y = -42.6846
FEATURE [TechDraw::DrawViewDimension] Dimension010
  Arbitrary = false
  FormatSpec = (Note-4) ⌀%.2f
  Inverted = false
  LockPosition = false
  MeasureType = 1
  OverTolerance = 0
  References2D = -> [DrawViewSection001]
  Rotation = 0
  ScaleType = 0
  TheoreticalExact = false
  Type = 5
  UnderTolerance = 0
  X = 22.8922
  Y = 77.6878
FEATURE [TechDraw::DrawViewDimension] Dimension011
  Arbitrary = false
  FormatSpec = (Note-5) %.2f
  Inverted = false
  LockPosition = false
  MeasureType = 1
  OverTolerance = 0
  References2D = -> [DrawViewSection001]
  Rotation = 0
  ScaleType = 0
  TheoreticalExact = false
  Type = 2
  UnderTolerance = 0
  X = 25.5908
  Y = 39.7969
FEATURE [TechDraw::DrawViewBalloon] Balloon002
  EndType = 0
  LockPosition = false
  OriginIsSet = false
  OriginX = 17.1497
  OriginY = -411.202
  Rotation = 0
  ScaleType = 0
  Symbol = 6
  SymbolScale = 1
  Text = Note-3
  TextWrapLen = -1
  X = -14.0893
  Y = 64.8829
  sourceView = -> View
FEATURE [TechDraw::DrawViewDimension] Dimension012
  Arbitrary = false
  FormatSpec = %.2f
  Inverted = false
  LockPosition = false
  MeasureType = 1
  OverTolerance = 0.1
  References2D = -> [DrawViewSection001]
  Rotation = 0
  ScaleType = 0
  TheoreticalExact = false
  Type = 1
  UnderTolerance = -0.1
  X = -7.84548
  Y = -85.3097
FEATURE [TechDraw::DrawPage] Page
  KeepUpdated = true
  NextBalloonIndex = 4
  ProjectionType = 0
  Template = -> Template
  Views = -> [ProjGroup,DrawViewSection,View,Annotation001,Dimension,Dimension001,Dimension002,Dimension003,Dimension004,Symbol,Dimension006,Dimension007,Balloon,Balloon001,Symbol001,Annotation002,DrawViewSection001,Dimension008,Dimension009,Dimension010,Dimension011,Balloon002,Dimension012]
PROVENANCE & LICENSES
A FreeCAD (.FCStd) document from a public repository crawl; recipes are the document's own serialized feature recipes (and, for linked parts, companion documents' recipes).
License: lgpl-3.0.
